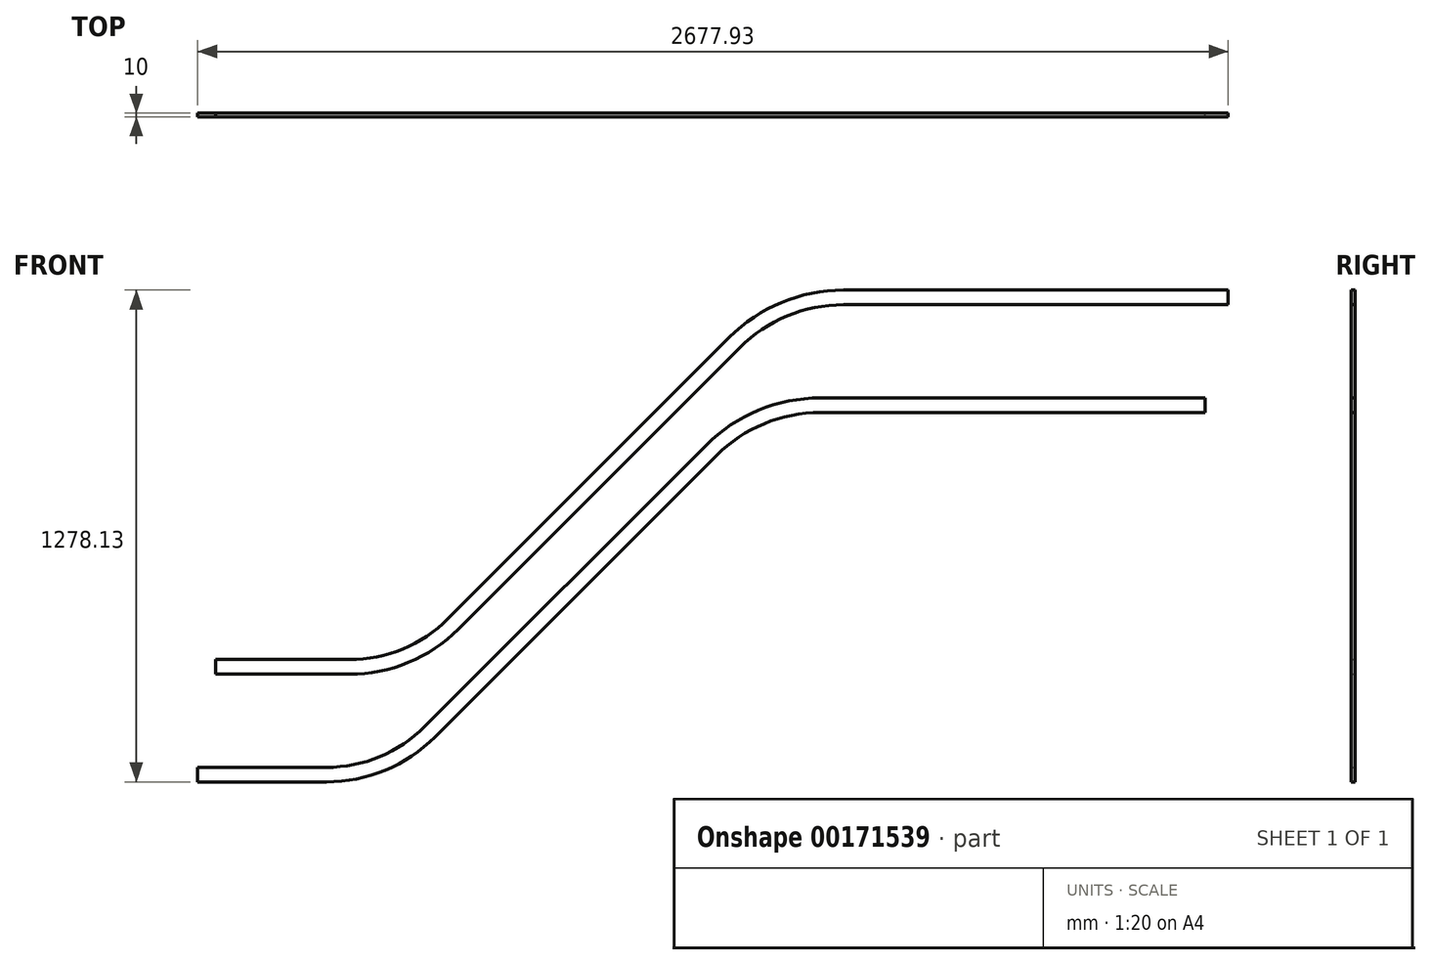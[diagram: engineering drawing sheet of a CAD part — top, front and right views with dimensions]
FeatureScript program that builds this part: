
annotation { "Feature Type Name" : "Feature", "Feature Type Description" : "" }
export const myFeature = defineFeature(function(context is Context, id is Id, definition is map)
    precondition{}
    {
        {
            var Q0;
            Q0=qCreatedBy(makeId("Front.planeOp"),FACE);
            var sketch = newSketch(context, id + "F0", { "sketchPlane" : qUnion([Q0])});
            skLineSegment(sketch, "E0", {"start": v(0, 0) * mm, "end": v(848.53, 848.53) * mm, "construction": true});
            skLineSegment(sketch, "E1", {"start": v(0, 0) * mm, "end": v(0, 220) * mm, "construction": true});
            skLineSegment(sketch, "E2", {"start": v(0, 220) * mm, "end": v(818.53, 1038.53) * mm, "construction": true});
            skLineSegment(sketch, "E3", {"start": v(818.53, 1038.53) * mm, "end": v(818.53, 818.53) * mm, "construction": true});
            skLineSegment(sketch, "E4", {"start": v(818.53, 1038.53) * mm, "end": v(805.1, 1051.96) * mm});
            skLineSegment(sketch, "E5", {"start": v(0, 220) * mm, "end": v(-13.44, 233.44) * mm});
            skLineSegment(sketch, "E6", {"start": v(897.57, 1139.49) * mm, "end": v(807.57, 1049.49) * mm});
            skLineSegment(sketch, "E7", {"start": v(0, 0) * mm, "end": v(-13.44, 13.44) * mm});
            skLineSegment(sketch, "E8", {"start": v(835.1, 861.96) * mm, "end": v(103.72, 130.6) * mm});
            skPoint(sketch, "E9", {"position": v(-10.96, 10.96) * mm});
            skPoint(sketch, "E10", {"position": v(807.57, 829.49) * mm});
            skLineSegment(sketch, "E11", {"start": v(837.57, 859.49) * mm, "end": v(792.59, 814.5) * mm});
            skLineSegment(sketch, "E12", {"start": v(0, 0) * mm, "end": v(818.53, 0) * mm, "construction": true});
            skLineSegment(sketch, "E13", {"start": v(818.53, 1038.53) * mm, "end": v(908.53, 1128.53) * mm, "construction": true});
            skArc(sketch, "E14", {"start": v(1191.37, 1245.69) * mm, "mid": v(1038.3, 1215.24) * mm, "end": v(908.53, 1128.53) * mm, "construction": true});
            skLineSegment(sketch, "E15", {"start": v(1191.37, 1245.69) * mm, "end": v(2191.37, 1245.69) * mm, "construction": true});
            skArc(sketch, "E16.trimOffspring", {"start": v(792.25, 819.12) * mm, "mid": v(793.26, 806.86) * mm, "end": v(794.64, 794.64) * mm, "construction": true});
            skLineSegment(sketch, "E17", {"start": v(908.53, 1128.53) * mm, "end": v(895.1, 1141.96) * mm});
            skArc(sketch, "E18.0", {"start": v(1191.37, 1264.69) * mm, "mid": v(1031.03, 1232.8) * mm, "end": v(895.1, 1141.96) * mm});
            skArc(sketch, "E19.0", {"start": v(1191.36, 1261.19) * mm, "mid": v(1032.36, 1229.56) * mm, "end": v(897.57, 1139.49) * mm});
            skLineSegment(sketch, "E20", {"start": v(1191.36, 1264.69) * mm, "end": v(2191.37, 1264.69) * mm});
            skLineSegment(sketch, "E21", {"start": v(1191.37, 1264.69) * mm, "end": v(2191.37, 1264.69) * mm});
            skLineSegment(sketch, "E22", {"start": v(2191.37, 1264.69) * mm, "end": v(2191.37, 1245.69) * mm});
            skLineSegment(sketch, "E23.MirrorCS", {"start": v(0, 220) * mm, "end": v(13.44, 206.56) * mm});
            skLineSegment(sketch, "E24.MirrorCS", {"start": v(190.6, 383.72) * mm, "end": v(921.96, 1115.1) * mm});
            skLineSegment(sketch, "E25.MirrorCS", {"start": v(1191.37, 1226.69) * mm, "end": v(2191.37, 1226.69) * mm});
            skLineSegment(sketch, "E26.MirrorCS", {"start": v(2191.37, 1226.69) * mm, "end": v(2191.37, 1245.69) * mm});
            skLineSegment(sketch, "E27.MirrorCS", {"start": v(0, 0) * mm, "end": v(13.44, -13.44) * mm});
            skLineSegment(sketch, "E28.MirrorCS", {"start": v(861.96, 835.1) * mm, "end": v(130.6, 103.72) * mm});
            skArc(sketch, "E29.0", {"start": v(1191.37, 1226.69) * mm, "mid": v(1045.57, 1197.68) * mm, "end": v(921.96, 1115.1) * mm});
            skLineSegment(sketch, "E30", {"start": v(1191.36, 1261.19) * mm, "end": v(2191.37, 1261.19) * mm});
            skLineSegment(sketch, "E31", {"start": v(2285.84, 965.69) * mm, "end": v(1131.37, 965.69) * mm, "construction": true});
            skPoint(sketch, "E32.visualSharp", {"position": v(965.69, 965.69) * mm});
            skArc(sketch, "E32.filletArc", {"start": v(1131.37, 965.69) * mm, "mid": v(978.3, 935.24) * mm, "end": v(848.53, 848.53) * mm, "construction": true});
            skPoint(sketch, "E33.orphan", {"position": v(831.96, 805.1) * mm});
            skPoint(sketch, "E34.orphan", {"position": v(805.1, 831.96) * mm});
            skLineSegment(sketch, "E35", {"start": v(848.53, 848.53) * mm, "end": v(835.1, 861.96) * mm});
            skLineSegment(sketch, "E36", {"start": v(848.53, 848.53) * mm, "end": v(861.96, 835.1) * mm});
            skLineSegment(sketch, "E37", {"start": v(1131.37, 965.69) * mm, "end": v(1131.37, 984.69) * mm});
            skLineSegment(sketch, "E38", {"start": v(1131.37, 965.69) * mm, "end": v(1131.37, 946.69) * mm});
            skLineSegment(sketch, "E39", {"start": v(1131.37, 984.69) * mm, "end": v(2131.37, 984.69) * mm});
            skLineSegment(sketch, "E40", {"start": v(1131.37, 946.69) * mm, "end": v(2131.37, 946.69) * mm});
            skArc(sketch, "E41.0", {"start": v(1131.37, 984.69) * mm, "mid": v(971.03, 952.8) * mm, "end": v(835.1, 861.96) * mm});
            skArc(sketch, "E42.0", {"start": v(1131.37, 946.69) * mm, "mid": v(985.57, 917.68) * mm, "end": v(861.96, 835.1) * mm});
            skLineSegment(sketch, "E43", {"start": v(2131.37, 946.69) * mm, "end": v(2131.37, 984.69) * mm});
            skLineSegment(sketch, "E44", {"start": v(0, 0) * mm, "end": v(-390.76, 0) * mm, "construction": true});
            skLineSegment(sketch, "E45", {"start": v(-152.25, -13.44) * mm, "end": v(-486.56, -13.44) * mm});
            skPoint(sketch, "E46.visualSharp", {"position": v(13.44, -13.44) * mm});
            skArc(sketch, "E46.filletArc", {"start": v(-152.25, -13.44) * mm, "mid": v(0.82, 17.01) * mm, "end": v(130.6, 103.72) * mm});
            skArc(sketch, "E47.0", {"start": v(-152.25, 24.56) * mm, "mid": v(-13.72, 52.12) * mm, "end": v(103.72, 130.6) * mm});
            skLineSegment(sketch, "E48", {"start": v(-152.25, 24.56) * mm, "end": v(-486.56, 24.56) * mm});
            skPoint(sketch, "E49.end.orphan", {"position": v(-486.56, 13.44) * mm});
            skLineSegment(sketch, "E50", {"start": v(-486.56, 24.56) * mm, "end": v(-486.56, -13.44) * mm});
            skPoint(sketch, "E51", {"position": v(60, 280) * mm});
            skLineSegment(sketch, "E52", {"start": v(60, 280) * mm, "end": v(-440, 280) * mm, "construction": true});
            skPoint(sketch, "E53.trimOffspring.end.orphan", {"position": v(-10.96, 230.96) * mm});
            skLineSegment(sketch, "E54", {"start": v(-92.25, 266.56) * mm, "end": v(-440, 266.56) * mm});
            skPoint(sketch, "E55.newPointB", {"position": v(13.44, 206.56) * mm});
            skArc(sketch, "E55.filletArc", {"start": v(-92.25, 266.56) * mm, "mid": v(60.82, 297.01) * mm, "end": v(190.6, 383.72) * mm});
            skArc(sketch, "E56.0", {"start": v(-92.25, 304.56) * mm, "mid": v(46.28, 332.12) * mm, "end": v(163.72, 410.6) * mm});
            skLineSegment(sketch, "E57", {"start": v(-92.25, 304.56) * mm, "end": v(-105.13, 304.56) * mm});
            skLineSegment(sketch, "E58", {"start": v(-440, 266.56) * mm, "end": v(-440, 304.56) * mm});
            skLineSegment(sketch, "E59", {"start": v(-440, 304.56) * mm, "end": v(-92.25, 304.56) * mm});
            skLineSegment(sketch, "E60.trimOffspring", {"start": v(163.72, 410.6) * mm, "end": v(895.1, 1141.96) * mm});
            skSolve(sketch);
        }
        {
            var Q0;
            {var subQ7=sQuery(id+"F0.wireOp",EDGE,"E19.0");Q0=makeQuery(id+"F0.imprint","IMPRINT",FACE,{"disambiguationData":[TD([[makeQuery(id+"F0.imprint","IMPRINT",EDGE,{"derivedFrom":subQ7}),1.0]])]});}
            var Q1;
            {var subQ2=sQuery(id+"F0.wireOp",EDGE,"E11");Q1=makeQuery(id+"F0.imprint","IMPRINT",FACE,{"disambiguationData":[TD([[makeQuery(id+"F0.imprint","IMPRINT",EDGE,{"derivedFrom":subQ2}),1.0]])]});}
            var Q2;
            {var subQ0=sQuery(id+"F0.wireOp",EDGE,"E8");Q2=makeQuery(id+"F0.imprint","IMPRINT",FACE,{"disambiguationData":[TD([[makeQuery(id+"F0.imprint","IMPRINT",EDGE,{"derivedFrom":subQ0}),1.0]])]});}
            var Q3;
            {var subQ0=sQuery(id+"F0.wireOp",EDGE,"AoN7KdMm-ffZk-X6zb-dTE1-4JXwBkCW7KrX");var subQ1=sQuery(id+"F0.wireOp",EDGE,"E4");var subQ2=makeQuery(id+"F0.imprint","INTERSECT",VERTEX,{"derivedFrom":[subQ1,subQ0]});Q3=makeQuery(id+"F0.imprint","IMPRINT",FACE,{"disambiguationData":[TD([[makeQuery(id+"F0.imprint","IMPRINT",EDGE,{"disambiguationData":[TD([[subQ2,1.0]])],"derivedFrom":subQ1}),1.0]])]});}
            var Q4;
            {var subQ1=sQuery(id+"F0.wireOp",EDGE,"E18.0");Q4=makeQuery(id+"F0.imprint","IMPRINT",FACE,{"disambiguationData":[TD([[makeQuery(id+"F0.imprint","IMPRINT",EDGE,{"derivedFrom":subQ1}),1.0]])]});}
            var Q5;
            {var subQ2=sQuery(id+"F0.wireOp",EDGE,"ylQYoBTy-uHQs-DUvq-hzLg-KdHwvXXQFkZA");Q5=makeQuery(id+"F0.imprint","IMPRINT",FACE,{"disambiguationData":[TD([[makeQuery(id+"F0.imprint","IMPRINT",EDGE,{"derivedFrom":subQ2}),1.0]])]});}
            var Q6;
            {var subQ0=sQuery(id+"F0.wireOp",EDGE,"ae3cefdc-d26c-48bc-819a-8258d35f30b8.0");Q6=makeQuery(id+"F0.imprint","IMPRINT",FACE,{"disambiguationData":[TD([[makeQuery(id+"F0.imprint","IMPRINT",EDGE,{"derivedFrom":subQ0}),1.0]])]});}
            var Q7;
            {var subQ0=sQuery(id+"F0.wireOp",EDGE,"AoN7KdMm-ffZk-X6zb-dTE1-4JXwBkCW7KrX");var subQ1=sQuery(id+"F0.wireOp",EDGE,"E4");var subQ2=makeQuery(id+"F0.imprint","INTERSECT",VERTEX,{"derivedFrom":[subQ1,subQ0]});Q7=makeQuery(id+"F0.imprint","IMPRINT",FACE,{"disambiguationData":[TD([[makeQuery(id+"F0.imprint","IMPRINT",EDGE,{"disambiguationData":[TD([[subQ2,1.0]])],"derivedFrom":subQ1}),-1.0]])]});}
            var Q8;
            {var subQ1=sQuery(id+"F0.wireOp",EDGE,"E36");Q8=makeQuery(id+"F0.imprint","IMPRINT",FACE,{"disambiguationData":[TD([[makeQuery(id+"F0.imprint","IMPRINT",EDGE,{"derivedFrom":subQ1}),1.0]])]});}
            var Q9;
            Q9=makeQuery(id+"F0.imprint","IMPRINT",FACE,{"disambiguationData":[TD([[makeQuery(id+"F0.imprint","IMPRINT",EDGE,{"derivedFrom":sQuery(id+"F0.wireOp",EDGE,"E37")}),-1.0]])]});
            extrude(context, id + "F1", {"entities" : qUnion([Q0, Q1, Q2, Q3, Q4, Q5, Q6, Q7, Q8, Q9]), "depth" : 10 * mm});
        }
    });
